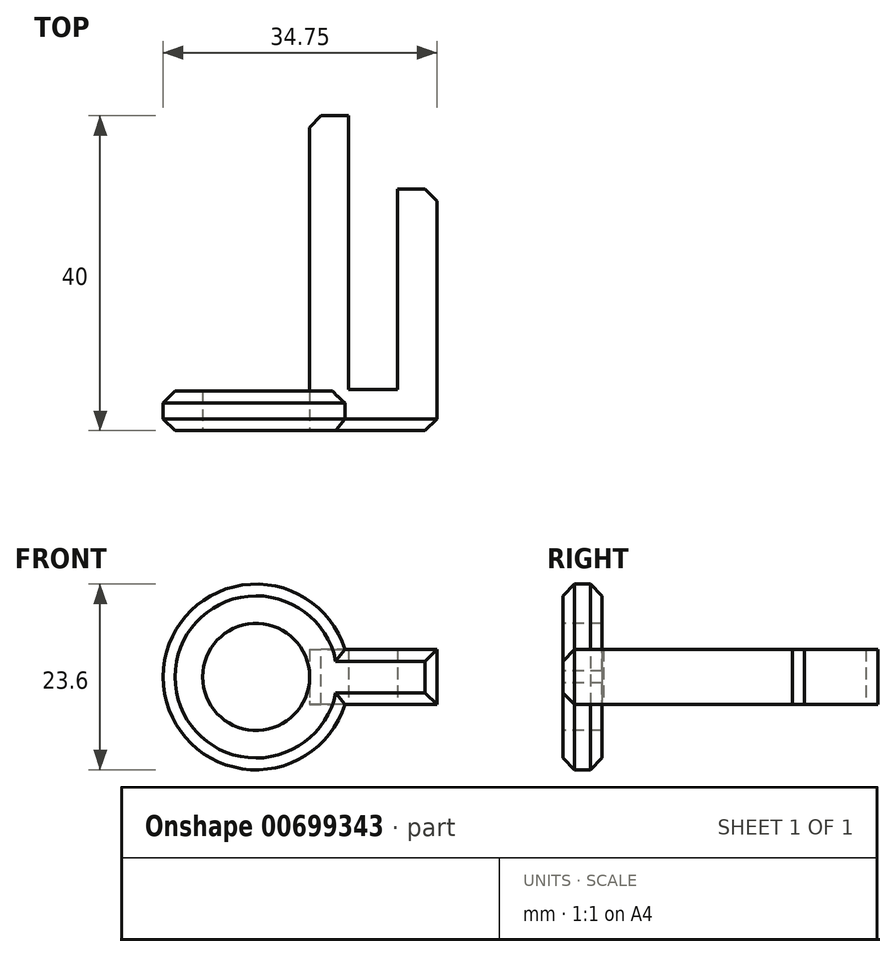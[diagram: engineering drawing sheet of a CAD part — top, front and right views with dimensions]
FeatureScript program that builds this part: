
annotation { "Feature Type Name" : "Feature", "Feature Type Description" : "" }
export const myFeature = defineFeature(function(context is Context, id is Id, definition is map)
    precondition{}
    {
        {
            var Q0;
            Q0=qCreatedBy(makeId("Top.planeOp"),FACE);
            var sketch = newSketch(context, id + "F0", { "sketchPlane" : qUnion([Q0])});
            skLineSegment(sketch, "E0", {"start": v(0, 40) * mm, "end": v(0, 0) * mm});
            skLineSegment(sketch, "E1", {"start": v(0, 0) * mm, "end": v(16.2, 0) * mm});
            skLineSegment(sketch, "E2", {"start": v(16.2, 0) * mm, "end": v(16.2, 30.67) * mm});
            skLineSegment(sketch, "E3", {"start": v(16.2, 30.67) * mm, "end": v(11.2, 30.67) * mm});
            skLineSegment(sketch, "E4", {"start": v(11.2, 30.67) * mm, "end": v(11.2, 5.19) * mm});
            skLineSegment(sketch, "E5", {"start": v(11.2, 5.19) * mm, "end": v(5, 5.19) * mm});
            skLineSegment(sketch, "E6", {"start": v(5, 5.19) * mm, "end": v(5, 40) * mm});
            skLineSegment(sketch, "E7", {"start": v(5, 40) * mm, "end": v(0, 40) * mm});
            skSolve(sketch);
        }
        {
            var Q0;
            Q0=qCreatedBy(makeId("Front.planeOp"),FACE);
            var sketch = newSketch(context, id + "F1", { "sketchPlane" : qUnion([Q0])});
            skCircle(sketch, "E8", {"center": v(-6.76, 0) * mm, "radius": 11.8 * mm});
            skCircle(sketch, "E9", {"center": v(-6.76, 0) * mm, "radius": 6.8 * mm});
            skSolve(sketch);
        }
        {
            var Q0;
            Q0=makeQuery(id+"F0.imprint","IMPRINT",FACE,{"disambiguationData":[TD([[makeQuery(id+"F0.imprint","IMPRINT",EDGE,{"derivedFrom":sQuery(id+"F0.wireOp",EDGE,"E0")}),1.0]])]});
            extrude(context, id + "F2", {"entities" : qUnion([Q0]), "endBound" : BoundingType.SYMMETRIC, "depth" : 7 * mm, "offsetDistance" : 25 * mm});
        }
        {
            var Q0;
            Q0=makeQuery(id+"F1.imprint","IMPRINT",FACE,{"disambiguationData":[TD([[makeQuery(id+"F1.imprint","IMPRINT",EDGE,{"derivedFrom":sQuery(id+"F1.wireOp",EDGE,"E8")}),1.0]])]});
            extrude(context, id + "F3", {"entities" : qUnion([Q0]), "operationType" : NewBodyOperationType.ADD, "depth" : -5 * mm, "offsetDistance" : 25 * mm});
        }
        {
            var Q0;
            Q0=makeQuery(id+"F3.opExtrude","CAP_EDGE",EDGE,{"disambiguationData":[OSD([sQuery(id+"F1.wireOp",EDGE,"E8")])],"isStart":true});
            var Q1;
            Q1=makeQuery(id+"F3.opExtrude","CAP_EDGE",EDGE,{"disambiguationData":[OSD([sQuery(id+"F1.wireOp",EDGE,"E8")])],"isStart":false});
            var Q2;
            Q2=makeQuery(id+"F2.opExtrude","SWEPT_EDGE",EDGE,{"disambiguationData":[OSD([sQuery(id+"F0.wireOp",EDGE,"E1"),sQuery(id+"F0.wireOp",EDGE,"E2")])]});
            var Q3;
            Q3=makeQuery(id+"F2.opExtrude","CAP_EDGE",EDGE,{"disambiguationData":[OSD([sQuery(id+"F0.wireOp",EDGE,"E1")])],"isStart":true});
            var Q4;
            Q4=makeQuery(id+"F2.opExtrude","CAP_EDGE",EDGE,{"disambiguationData":[OSD([sQuery(id+"F0.wireOp",EDGE,"E1")])],"isStart":false});
            var Q5;
            Q5=makeQuery(id+"F2.opExtrude","SWEPT_EDGE",EDGE,{"disambiguationData":[OSD([sQuery(id+"F0.wireOp",EDGE,"E2"),sQuery(id+"F0.wireOp",EDGE,"E3")])]});
            var Q6;
            Q6=makeQuery(id+"F2.opExtrude","SWEPT_EDGE",EDGE,{"disambiguationData":[OSD([sQuery(id+"F0.wireOp",EDGE,"E0"),sQuery(id+"F0.wireOp",EDGE,"E7")])]});
            chamfer(context, id + "F4", {"entities" : qUnion([Q0, Q1, Q2, Q3, Q4, Q5, Q6]), "width" : 1.5 * mm, "tangentPropagation" : true});
        }
    });
